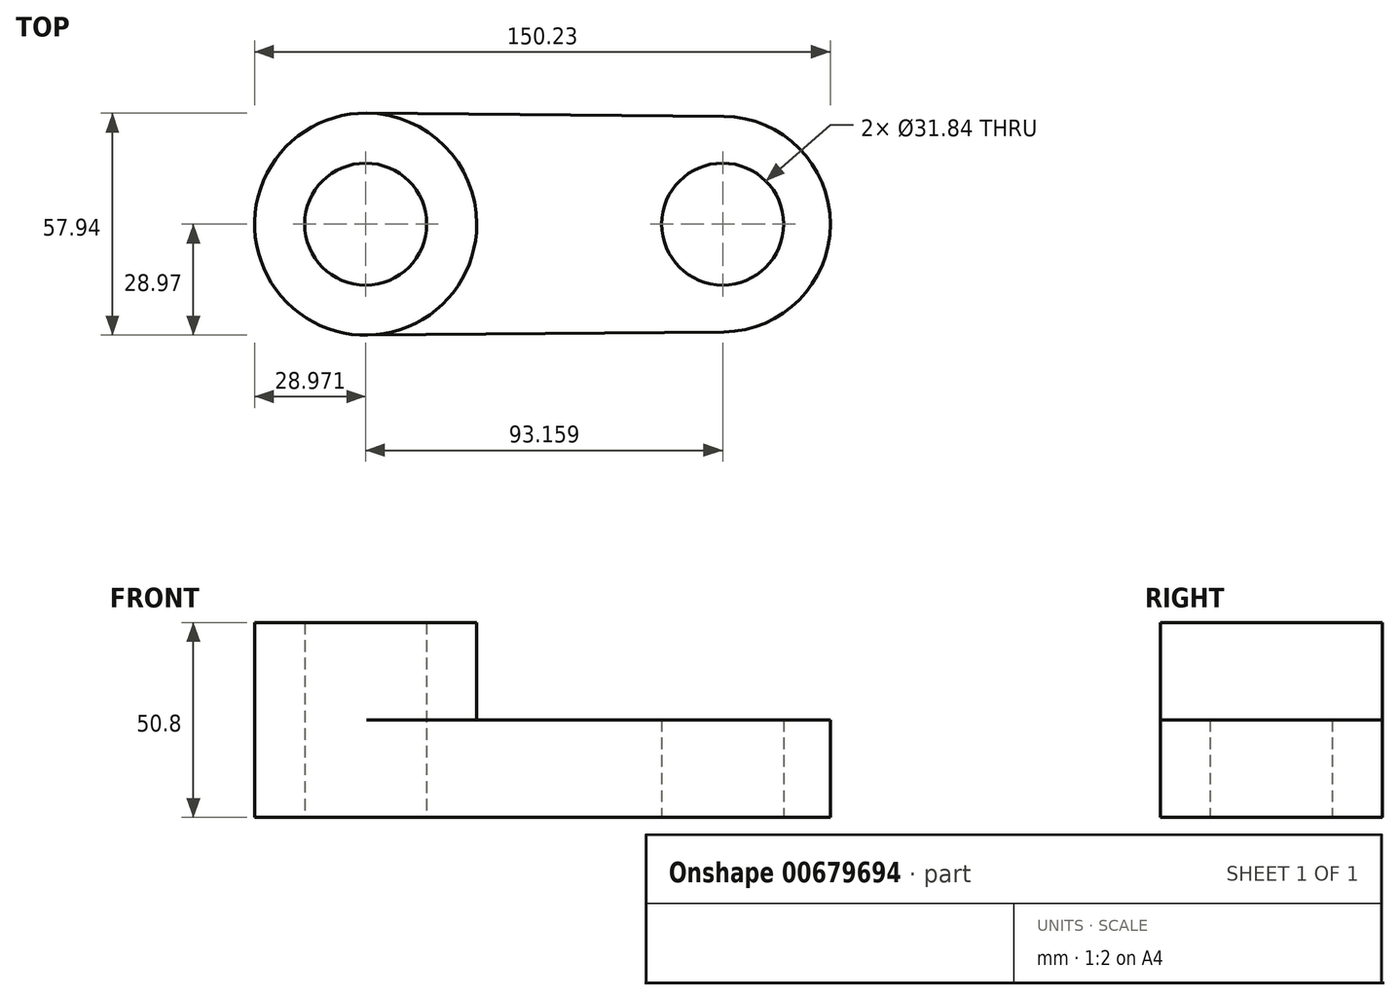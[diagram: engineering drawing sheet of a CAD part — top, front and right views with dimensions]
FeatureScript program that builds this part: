
annotation { "Feature Type Name" : "Feature", "Feature Type Description" : "" }
export const myFeature = defineFeature(function(context is Context, id is Id, definition is map)
    precondition{}
    {
        {
            var Q0;
            Q0=qCreatedBy(makeId("Top.planeOp"),FACE);
            var sketch = newSketch(context, id + "F0", { "sketchPlane" : qUnion([Q0])});
            skCircle(sketch, "E0", {"center": v(-46.58, 0) * mm, "radius": 15.92 * mm});
            skCircle(sketch, "E1", {"center": v(46.58, 0) * mm, "radius": 15.92 * mm});
            skArc(sketch, "E2", {"start": v(-46.3, 28.97) * mm, "mid": v(-75.55, 0) * mm, "end": v(-46.3, -28.97) * mm});
            skArc(sketch, "E3", {"start": v(46.84, -28.1) * mm, "mid": v(74.68, 0) * mm, "end": v(46.84, 28.1) * mm});
            skLineSegment(sketch, "E4", {"start": v(-46.3, 28.97) * mm, "end": v(46.84, 28.1) * mm});
            skLineSegment(sketch, "E5", {"start": v(46.84, -28.1) * mm, "end": v(-46.3, -28.97) * mm});
            skArc(sketch, "E6", {"start": v(-46.3, -28.97) * mm, "mid": v(-17.6, 0) * mm, "end": v(-46.3, 28.97) * mm});
            skSolve(sketch);
        }
        {
            var Q0;
            Q0=makeQuery(id+"F0.imprint","IMPRINT",FACE,{"disambiguationData":[TD([[makeQuery(id+"F0.imprint","IMPRINT",EDGE,{"derivedFrom":sQuery(id+"F0.wireOp",EDGE,"E1")}),-1.0]])]});
            var Q1;
            Q1=makeQuery(id+"F0.imprint","IMPRINT",FACE,{"disambiguationData":[TD([[makeQuery(id+"F0.imprint","IMPRINT",EDGE,{"derivedFrom":sQuery(id+"F0.wireOp",EDGE,"E0")}),-1.0]])]});
            extrude(context, id + "F1", {"entities" : qUnion([Q0, Q1]), "depth" : 25.4 * mm, "offsetDistance" : 25.4 * mm});
        }
        {
            var Q0;
            Q0=makeQuery(id+"F0.imprint","IMPRINT",FACE,{"disambiguationData":[TD([[makeQuery(id+"F0.imprint","IMPRINT",EDGE,{"derivedFrom":sQuery(id+"F0.wireOp",EDGE,"E0")}),-1.0]])]});
            extrude(context, id + "F2", {"entities" : qUnion([Q0]), "operationType" : NewBodyOperationType.ADD, "depth" : 50.8 * mm, "offsetDistance" : 25.4 * mm});
        }
    });
